# Revit family: Shower_Trim-DXV-Fitzgerald-D35160600_Series
name_source: partatom
category: Plumbing Fixtures
units: mm (PartAtom-declared; Revit-internal decimal feet)

## family parameters
Cut with Voids When Loaded = No
Host = Face
OmniClass Number = 23.45.05.14.17
OmniClass Title = Showers
Part Type = Normal
Room Calculation Point = No
Round Connector Dimension = Use Radius
Shared = Yes

## types (3) — shared parameters
ADA Compliant = Yes
Assembly Code = D2010710
CW Connection = No
CWFU = 3
Description = Fitzgerald Pressure Balanced Tub/Shower Valve Trim with Diverter
HW Connection = No
HWFU = 3
Height = 7 15/16"
Installation Instruction Link = https://dxv01.blob.core.windows.net
Installation Type = Wall Mounted
Length = 4 13/16"
Manufacturer = DXV
Price = Prices may vary. Please consult Manufacturer Representative for most up-to-date price list.
Product Documentation Link = https://dxv01.blob.core.windows.net
Product Page URL = https://www.dxv.com
Revised Date = 07/27/2021
URL = www.dxv.com
Vent Connection = No
WFU = 4
Warranty Documentation Link = https://www.dxv.com
Waste Connection = No
Width = 7 15/16"

## per-type parameters (varying)
| type | Default Elevation | Finish | Installation Height | Material |
| D35160600.100 | 48" | Brass-DXV-100-Polished Chrome | 48" | Brass-DXV-100-Polished Chrome |
| D35160600.150 | 50" | Brass-DXV-150-Platinum Nickel | 50" | Brass-DXV-150-Platinum Nickel |
| D35160600.144 | 48" | Brass-DXV-144-Brushed Nickel | 48" | Brass-DXV-144-Brushed Nickel |

note: column(s) folded — value = type name in every type: Model

## geometry (parser evidence)
native form markers: Sweep x2
no freeform markers — native parametric forms only
